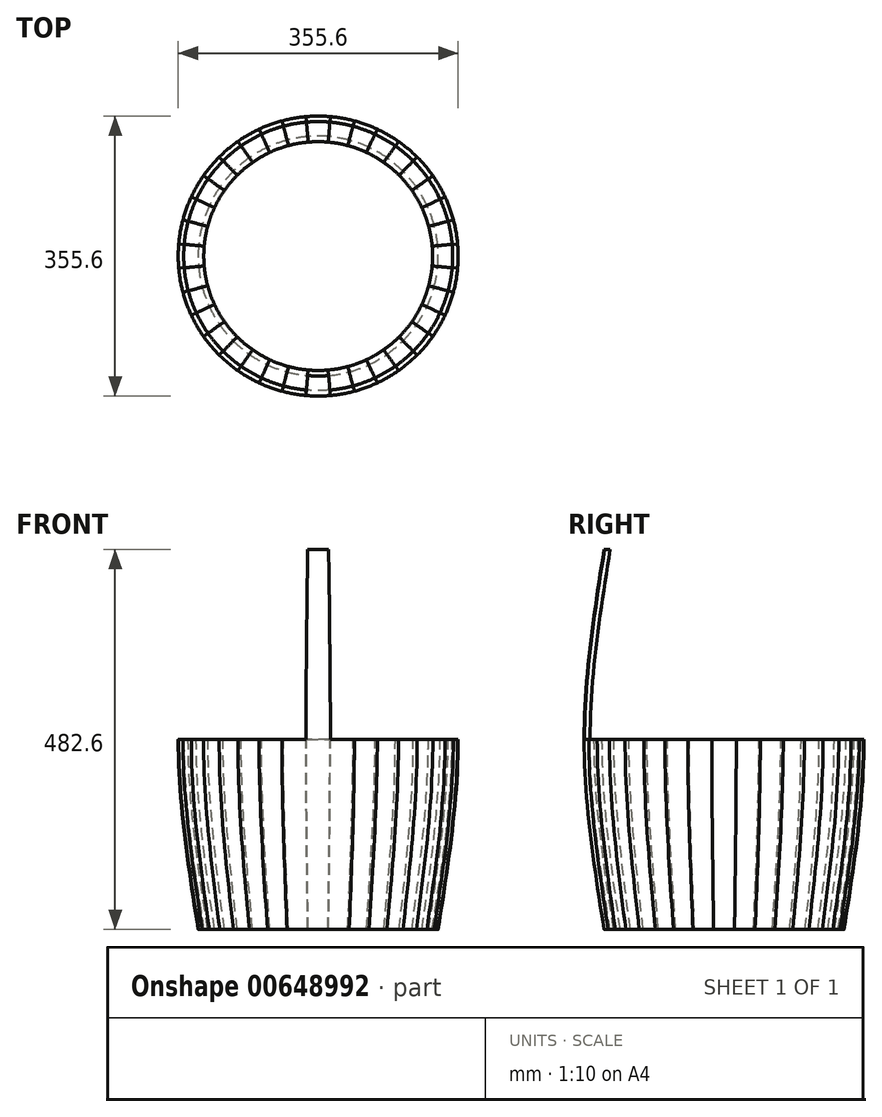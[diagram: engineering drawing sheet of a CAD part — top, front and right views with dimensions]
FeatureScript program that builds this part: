
annotation { "Feature Type Name" : "Feature", "Feature Type Description" : "" }
export const myFeature = defineFeature(function(context is Context, id is Id, definition is map)
    precondition{}
    {
        {
            var Q0;
            Q0=qCreatedBy(makeId("Top.planeOp"),FACE);
            var sketch = newSketch(context, id + "F0", { "sketchPlane" : qUnion([Q0])});
            skCircle(sketch, "E0", {"center": v(0, 0) * mm, "radius": 152.4 * mm});
            skSolve(sketch);
        }
        {
            var Q0;
            Q0=qCreatedBy(makeId("Top.planeOp"),FACE);
            cPlane(context, id + "F1", {"entities" : qUnion([Q0]), "cplaneType" : CPlaneType.OFFSET, "offset" : 241.3 * mm, "width" : 150 * mm, "height" : 150 * mm});
        }
        {
            var Q0;
            Q0=qCreatedBy(id+"F1.planeOp",FACE);
            var sketch = newSketch(context, id + "F2", { "sketchPlane" : qUnion([Q0])});
            skCircle(sketch, "E1", {"center": v(0, 0) * mm, "radius": 177.8 * mm});
            skSolve(sketch);
        }
        {
            var Q0;
            Q0=makeQuery(id+"F2.imprint","IMPRINT",FACE,{"disambiguationData":[TD([[makeQuery(id+"F2.imprint","IMPRINT",EDGE,{"derivedFrom":sQuery(id+"F2.wireOp",EDGE,"E1")}),1.0]])]});
            var Q1;
            Q1=makeQuery(id+"F0.imprint","IMPRINT",FACE,{"disambiguationData":[TD([[makeQuery(id+"F0.imprint","IMPRINT",EDGE,{"derivedFrom":sQuery(id+"F0.wireOp",EDGE,"E0")}),1.0]])]});
            loft(context, id + "F3", {"startCondition" : LoftEndDerivativeType.NORMAL_TO_PROFILE, "startMagnitude" : 1, "sheetProfilesArray" : [{ "sheetProfileEntities" : qUnion([Q0]) }, { "sheetProfileEntities" : qUnion([Q1]) }]});
        }
        {
            var Q0;
            Q0=makeQuery(id+"F3.opLoft","CAP_FACE",FACE,{"disambiguationData":[OSD([makeQuery(id+"F0.imprint","IMPRINT",FACE,{"disambiguationData":[TD([[makeQuery(id+"F0.imprint","IMPRINT",EDGE,{"derivedFrom":sQuery(id+"F0.wireOp",EDGE,"E0")}),1.0]])]})])],"isStart":true});
            var Q1;
            Q1=makeQuery(id+"F3.opLoft","CAP_FACE",FACE,{"disambiguationData":[OSD([makeQuery(id+"F2.imprint","IMPRINT",FACE,{"disambiguationData":[TD([[makeQuery(id+"F2.imprint","IMPRINT",EDGE,{"derivedFrom":sQuery(id+"F2.wireOp",EDGE,"E1")}),1.0]])]})])],"isStart":true});
            shell(context, id + "F4", {"entities" : qUnion([Q0, Q1]), "thickness" : 7 * mm});
        }
        {
            var Q0;
            Q0=qCreatedBy(makeId("Top.planeOp"),FACE);
            var sketch = newSketch(context, id + "F5", { "sketchPlane" : qUnion([Q0])});
            skPoint(sketch, "E2.center", {"position": v(0, 0) * mm});
            skArc(sketch, "E3", {"start": v(15.56, -177.8) * mm, "mid": v(0, 178.48) * mm, "end": v(-15.56, -177.8) * mm});
            skLineSegment(sketch, "E4", {"start": v(0, 0) * mm, "end": v(0, -177.8) * mm, "construction": true});
            skLineSegment(sketch, "E5", {"start": v(0, -177.8) * mm, "end": v(15.56, -177.8) * mm, "construction": true});
            skLineSegment(sketch, "E6", {"start": v(0, -177.8) * mm, "end": v(-15.56, -177.8) * mm, "construction": true});
            skLineSegment(sketch, "E7", {"start": v(0, 0) * mm, "end": v(-15.56, -177.8) * mm});
            skLineSegment(sketch, "E8", {"start": v(0, 0) * mm, "end": v(15.56, -177.8) * mm});
            skSolve(sketch);
        }
        {
            var Q0;
            Q0=makeQuery(id+"F5.imprint","IMPRINT",FACE,{"disambiguationData":[TD([[makeQuery(id+"F5.imprint","IMPRINT",EDGE,{"derivedFrom":sQuery(id+"F5.wireOp",EDGE,"6n4anIrU-655B-OWT2-d6l9-0ycdUH0Mrevo")}),1.0]])]});
            var Q1;
            Q1=makeQuery(id+"F5.imprint","IMPRINT",FACE,{"disambiguationData":[TD([[makeQuery(id+"F5.imprint","IMPRINT",EDGE,{"derivedFrom":sQuery(id+"F5.wireOp",EDGE,"E3")}),1.0]])]});
            extrude(context, id + "F6", {"entities" : qUnion([Q0, Q1]), "operationType" : NewBodyOperationType.REMOVE, "endBound" : BoundingType.THROUGH_ALL, "depth" : 25 * mm, "offsetDistance" : 25 * mm});
        }
        {
            var Q0;
            Q0=qCreatedBy(makeId("Right.planeOp"),FACE);
            var sketch = newSketch(context, id + "F7", { "sketchPlane" : qUnion([Q0])});
            skLineSegment(sketch, "E9", {"start": v(0, 0) * mm, "end": v(0, 404.17) * mm, "construction": true});
            skSolve(sketch);
        }
        {
            var Q0;
            Q0=makeQuery(id+"F3.opLoft","SWEPT_BODY",BODY,{"disambiguationData":[OSD([makeQuery(id+"F0.imprint","IMPRINT",FACE,{"disambiguationData":[TD([[makeQuery(id+"F0.imprint","IMPRINT",EDGE,{"derivedFrom":sQuery(id+"F0.wireOp",EDGE,"E0")}),1.0]])]}),makeQuery(id+"F2.imprint","IMPRINT",FACE,{"disambiguationData":[TD([[makeQuery(id+"F2.imprint","IMPRINT",EDGE,{"derivedFrom":sQuery(id+"F2.wireOp",EDGE,"E1")}),1.0]])]})])]});
            var Q1;
            Q1=sQuery(id+"F7.wireOp",EDGE,"E9");
            circularPattern(context, id + "F8", {"entities" : qUnion([Q0]), "axis" : qUnion([Q1]), "angle" : 360 * degree, "instanceCount" : 36, "equalSpace" : true});
        }
        {
            var Q0;
            Q0=makeQuery(id+"F3.opLoft","SWEPT_BODY",BODY,{"disambiguationData":[OSD([makeQuery(id+"F0.imprint","IMPRINT",FACE,{"disambiguationData":[TD([[makeQuery(id+"F0.imprint","IMPRINT",EDGE,{"derivedFrom":sQuery(id+"F0.wireOp",EDGE,"E0")}),1.0]])]}),makeQuery(id+"F2.imprint","IMPRINT",FACE,{"disambiguationData":[TD([[makeQuery(id+"F2.imprint","IMPRINT",EDGE,{"derivedFrom":sQuery(id+"F2.wireOp",EDGE,"E1")}),1.0]])]})])]});
            var Q1;
            Q1=makeQuery(id+"F3.opLoft","CAP_FACE",FACE,{"disambiguationData":[OSD([makeQuery(id+"F2.imprint","IMPRINT",FACE,{"disambiguationData":[TD([[makeQuery(id+"F2.imprint","IMPRINT",EDGE,{"derivedFrom":sQuery(id+"F2.wireOp",EDGE,"E1")}),1.0]])]})])],"isStart":true});
            mirror(context, id + "F9", {"operationType" : NewBodyOperationType.ADD, "entities" : qUnion([Q0]), "mirrorPlane" : qUnion([Q1])});
        }
    });
